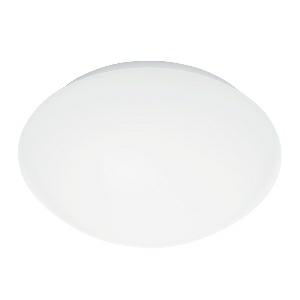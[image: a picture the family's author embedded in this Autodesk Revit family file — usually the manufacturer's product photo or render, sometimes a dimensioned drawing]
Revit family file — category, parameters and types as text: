
# Revit family: rs_pro_led_p2_056100
name_source: partatom
category: Leuchten
revit_build: Autodesk Revit 2016 (Build: 20190508_0715(x64)
units: mm (PartAtom-declared; Revit-internal decimal feet)

## family parameters
Basisbauteil = Fläche
Beim Laden mit Abzugskörper schneiden = Nein
Bemaßung runder Anschluss = Durchmesser verwenden
Gemeinsam genutzt = Nein
Lichtquelle = Nein
Raumberechnungspunkt = Nein
Teiletyp = Normal

## types (1)
- RS PRO LED P2 (1 x , 1730 lm, 3000 K)
    Beschreibung = Dimensions (Ø x H): 320 x 110 mm; Mains power supply: 220 – 240 V / 50 – 60 Hz; Sensor Technology: High frequency; Transmitter power: < 1 mW; HF-system: 5,8 GHz; Output: 16 W; Interconnection: Yes; Type of interconnection: Master/master; Luminous flux: 1730 lm; Colour temperature: 3000 K; Colour variation LED: SDCM3; Colour Rendering Index CRI: 80-89; With lamp: Yes, STEINEL LED system; Lamp: LED cannot be replaced; LED life expectancy (max. °C): 50000 h; Drop in luminous flux in accordance with LM80: L80B10; Base: without; LED cooling system: Passive Thermo Control; With motion detector: Yes; Detection: also through glass, wood and stud walls; Detection angle: 360 °; Angle of aperture: 160 °; Capability of masking out individual segments: Yes; Electronic scalability: Yes; Mechanical scalability: No; Reach, radial: Ø 8 m (50 m²); Reach, tangential: Ø 8 m (50 m²); Continuous light: selectable, 4h; Photo-cell controller: Yes; Twilight setting: 2 – 2000 lx; Time setting: 5 sec – 15 min; Basic light level function: Yes; Basic light level function time: 10/30 min, all night; Soft light start: Yes; Impact resistance: IK03; IP-rating: IP54; Protection class: II; Ambient temperature: 10 – 40 °C; Housing material: Plastic; Cover material: Plastic, opal; Manufacturer's Warranty: 5 years; Settings via: Potentiometers; With remote control: No; Version: warm white; PU1, EAN: 4007841056100
    CIE Flux Codes = 39 68 87 86 100
    Color Rendering = 80-89
    Color Temperature = 3000 K
    Frequency = 50 Hz, 60 Hz
    Height = 0 mm  [stored 0 ft]
    Hersteller = Steinel
    Lamp Light Flux = 1730 lm
    Lamp count = 1
    Lampe = 1 x
    Length = 320 mm
    Luminous efficacy = 108 lm/W
    ModVariant = Nein
    Modell = 056100
    Mounting Type = Surface mounted
    Number of Poles = 1
    OnlyDefault = Ja
    Power Factor = 1
    Product Name = RS PRO LED P2
    Product group = Sensor-switched indoor light
    ProductGroupID = 30
    Protection Class = Protection class II
    Protection Degree = IP 54
    RlxData = <blob elided: 37737 chars, md5=28025e3d>
    Scheinlast = 16 VA
    Socket = socket
    Standby Power = 0 W
    System Light Flux = 1730 lm
    System Power = 16 W
    Typenbild = produkt1_056100.jpg
    Typenkommentare = Product without accessories
    URL = http://relux.com
    VarID = ---
    Voltage = 0 V
    Vorgabe-Ansicht = 1800 mm
    Weight = 0.00 kg
    Width = 0 mm  [stored 0 ft]

note: [stored X ft] marks values corroborated as IEEE doubles in the binary element streams (Revit-internal decimal feet)

## geometry (parser evidence)
native form markers: Sweep x15
no freeform markers — native parametric forms only
